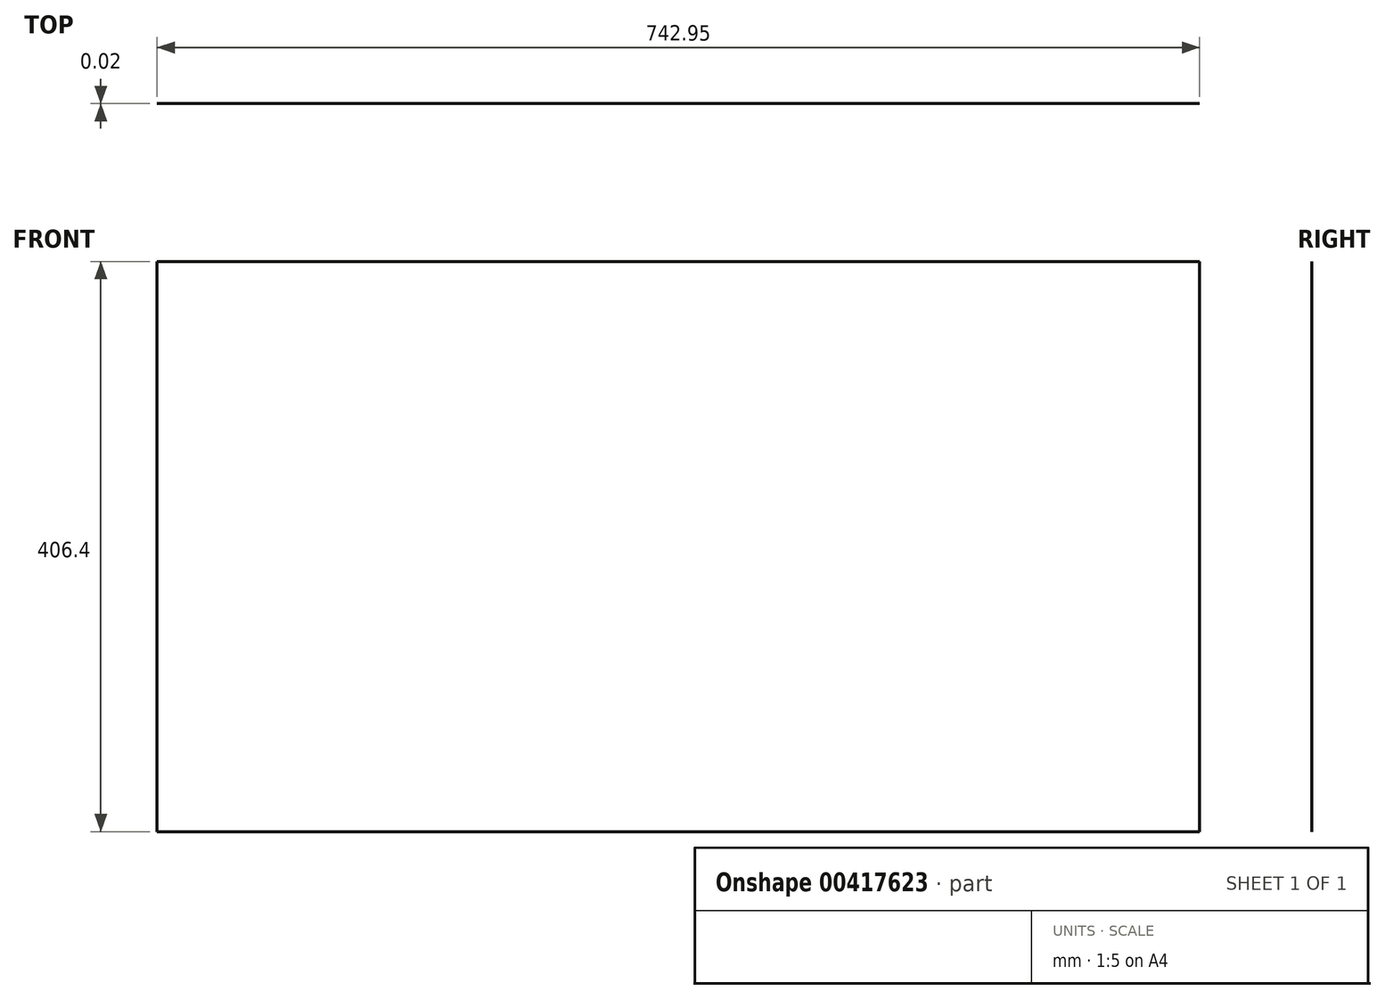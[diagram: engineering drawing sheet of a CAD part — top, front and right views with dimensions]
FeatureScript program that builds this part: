
annotation { "Feature Type Name" : "Feature", "Feature Type Description" : "" }
export const myFeature = defineFeature(function(context is Context, id is Id, definition is map)
    precondition{}
    {
        {
            var Q0;
            Q0=qCreatedBy(makeId("Front.planeOp"),FACE);
            var sketch = newSketch(context, id + "F0", { "sketchPlane" : qUnion([Q0])});
            skLineSegment(sketch, "E0.bottom", {"start": v(0, 0) * mm, "end": v(742.95, 0) * mm});
            skLineSegment(sketch, "E0.top", {"start": v(0, 406.4) * mm, "end": v(742.95, 406.4) * mm});
            skLineSegment(sketch, "E0.left", {"start": v(0, 0) * mm, "end": v(0, 406.4) * mm});
            skLineSegment(sketch, "E0.right", {"start": v(742.95, 0) * mm, "end": v(742.95, 406.4) * mm});
            skSolve(sketch);
        }
        {
            var Q0;
            Q0=makeQuery(id+"F0.imprint","IMPRINT",FACE,{"disambiguationData":[TD([[makeQuery(id+"F0.imprint","IMPRINT",EDGE,{"derivedFrom":sQuery(id+"F0.wireOp",EDGE,"E0.bottom")}),1.0]])]});
            extrude(context, id + "F1", {"entities" : qUnion([Q0]), "depth" : 5 / 203.2 * mm});
        }
    });
